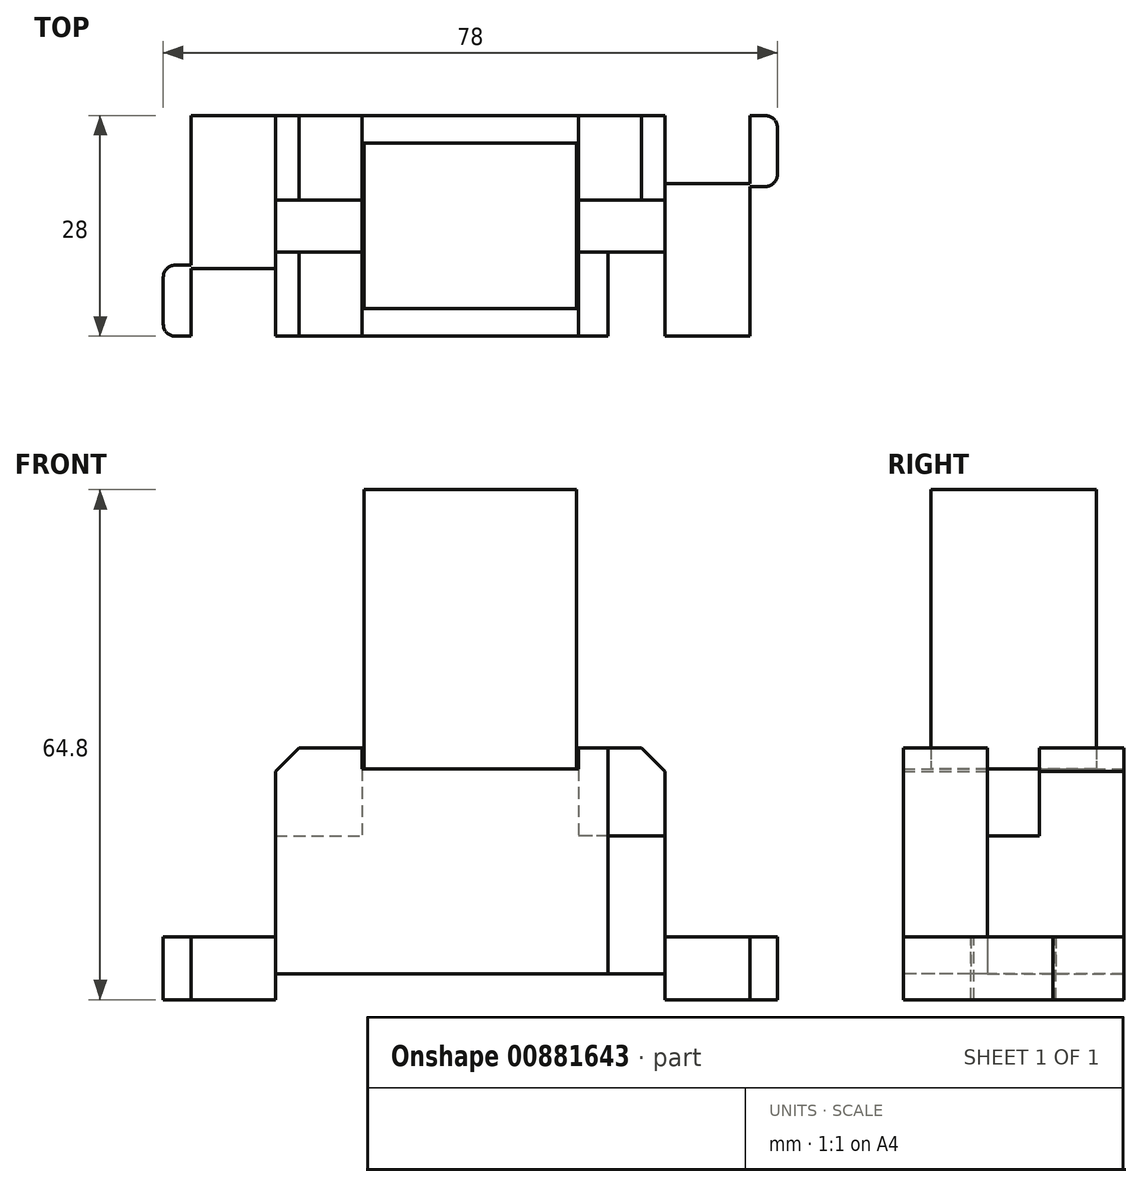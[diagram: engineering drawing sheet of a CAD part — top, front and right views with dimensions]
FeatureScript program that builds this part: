
annotation { "Feature Type Name" : "Feature", "Feature Type Description" : "" }
export const myFeature = defineFeature(function(context is Context, id is Id, definition is map)
    precondition{}
    {
        {
            var Q0;
            Q0=qCreatedBy(makeId("Top.planeOp"),FACE);
            var sketch = newSketch(context, id + "F0", { "sketchPlane" : qUnion([Q0])});
            skLineSegment(sketch, "E0.bottom", {"start": v(0, 0) * mm, "end": v(71, 0) * mm});
            skLineSegment(sketch, "E0.top", {"start": v(0, 28) * mm, "end": v(71, 28) * mm});
            skLineSegment(sketch, "E0.left", {"start": v(0, 0) * mm, "end": v(0, 28) * mm});
            skLineSegment(sketch, "E0.right", {"start": v(71, 0) * mm, "end": v(71, 28) * mm});
            skLineSegment(sketch, "E1.left", {"start": v(0, 28) * mm, "end": v(0, 19) * mm});
            skLineSegment(sketch, "E2.left", {"start": v(71, 0) * mm, "end": v(71, 9) * mm});
            skLineSegment(sketch, "E3", {"start": v(53, 28) * mm, "end": v(53, 0) * mm});
            skLineSegment(sketch, "E4", {"start": v(0, 14) * mm, "end": v(71, 14) * mm, "construction": true});
            skLineSegment(sketch, "E5", {"start": v(35.5, 28) * mm, "end": v(35.5, 0) * mm, "construction": true});
            skLineSegment(sketch, "E6.MirrorCS", {"start": v(18, 28) * mm, "end": v(18, 0) * mm});
            skLineSegment(sketch, "E7.bottom", {"start": v(71, 0) * mm, "end": v(60.25, 0) * mm});
            skLineSegment(sketch, "E7.top", {"start": v(71, 19.4) * mm, "end": v(60.25, 19.4) * mm});
            skLineSegment(sketch, "E7.left", {"start": v(71, 0) * mm, "end": v(71, 19.4) * mm});
            skLineSegment(sketch, "E7.right", {"start": v(60.25, 0) * mm, "end": v(60.25, 19.4) * mm});
            skLineSegment(sketch, "E8.bottom", {"start": v(0, 28) * mm, "end": v(10.75, 28) * mm});
            skLineSegment(sketch, "E8.top", {"start": v(0, 8.6) * mm, "end": v(10.75, 8.6) * mm});
            skLineSegment(sketch, "E8.left", {"start": v(0, 28) * mm, "end": v(0, 8.6) * mm});
            skLineSegment(sketch, "E8.right", {"start": v(10.75, 28) * mm, "end": v(10.75, 8.6) * mm});
            skLineSegment(sketch, "E9.MirrorCS", {"start": v(0, 9) * mm, "end": v(-3.5, 9) * mm});
            skLineSegment(sketch, "E10.MirrorCS", {"start": v(-3.5, 0) * mm, "end": v(-3.5, 9) * mm});
            skLineSegment(sketch, "E11.MirrorCS", {"start": v(0, 0) * mm, "end": v(-3.5, 0) * mm});
            skLineSegment(sketch, "E12.MirrorCS", {"start": v(71, 19) * mm, "end": v(74.5, 19) * mm});
            skLineSegment(sketch, "E13.MirrorCS", {"start": v(74.5, 28) * mm, "end": v(74.5, 19) * mm});
            skLineSegment(sketch, "E14.MirrorCS", {"start": v(71, 28) * mm, "end": v(74.5, 28) * mm});
            skLineSegment(sketch, "E15.bottom", {"start": v(60.25, 0) * mm, "end": v(49.25, 0) * mm});
            skLineSegment(sketch, "E15.top", {"start": v(60.25, 10.7) * mm, "end": v(49.25, 10.7) * mm});
            skLineSegment(sketch, "E15.left", {"start": v(60.25, 0) * mm, "end": v(60.25, 10.7) * mm});
            skLineSegment(sketch, "E15.right", {"start": v(49.25, 0) * mm, "end": v(49.25, 10.7) * mm});
            skLineSegment(sketch, "E16.MirrorCS", {"start": v(21.75, 0) * mm, "end": v(21.75, 10.7) * mm});
            skLineSegment(sketch, "E17.MirrorCS", {"start": v(10.75, 10.7) * mm, "end": v(21.75, 10.7) * mm});
            skLineSegment(sketch, "E18.MirrorCS", {"start": v(10.75, 17.3) * mm, "end": v(21.75, 17.3) * mm});
            skLineSegment(sketch, "E19.MirrorCS", {"start": v(21.75, 28) * mm, "end": v(21.75, 17.3) * mm});
            skLineSegment(sketch, "E20.MirrorCS", {"start": v(60.25, 17.3) * mm, "end": v(49.25, 17.3) * mm});
            skLineSegment(sketch, "E21.MirrorCS", {"start": v(49.25, 28) * mm, "end": v(49.25, 17.3) * mm});
            skLineSegment(sketch, "E22", {"start": v(10.75, 8.6) * mm, "end": v(10.75, 0) * mm});
            skLineSegment(sketch, "E23", {"start": v(60.25, 19.4) * mm, "end": v(60.25, 28) * mm});
            skLineSegment(sketch, "E24", {"start": v(49.25, 17.3) * mm, "end": v(49.25, 10.7) * mm});
            skLineSegment(sketch, "E25", {"start": v(21.75, 17.3) * mm, "end": v(21.75, 10.7) * mm});
            skLineSegment(sketch, "E26.bottom", {"start": v(22, 24.5) * mm, "end": v(49, 24.5) * mm});
            skLineSegment(sketch, "E26.top", {"start": v(22, 3.5) * mm, "end": v(49, 3.5) * mm});
            skLineSegment(sketch, "E26.left", {"start": v(22, 24.5) * mm, "end": v(22, 3.5) * mm});
            skLineSegment(sketch, "E26.right", {"start": v(49, 24.5) * mm, "end": v(49, 3.5) * mm});
            skPoint(sketch, "E26.middle", {"position": v(35.5, 14) * mm});
            skSolve(sketch);
        }
        {
            var Q0;
            {var subQ1=sQuery(id+"F0.wireOp",EDGE,"E0.left");Q0=makeQuery(id+"F0.imprint","IMPRINT",FACE,{"disambiguationData":[TD([[makeQuery(id+"F0.imprint","IMPRINT",EDGE,{"derivedFrom":subQ1}),1.0]])]});}
            var Q1;
            {var subQ0=sQuery(id+"F0.wireOp",EDGE,"E0.left");Q1=makeQuery(id+"F0.imprint","IMPRINT",FACE,{"disambiguationData":[TD([[makeQuery(id+"F0.imprint","IMPRINT",EDGE,{"derivedFrom":subQ0}),-1.0]])]});}
            var Q2;
            {var subQ3=sQuery(id+"F0.wireOp",EDGE,"E8.bottom");Q2=makeQuery(id+"F0.imprint","IMPRINT",FACE,{"disambiguationData":[TD([[makeQuery(id+"F0.imprint","IMPRINT",EDGE,{"derivedFrom":subQ3}),-1.0]])]});}
            var Q3;
            {var subQ2=sQuery(id+"F0.wireOp",EDGE,"E0.right");Q3=makeQuery(id+"F0.imprint","IMPRINT",FACE,{"disambiguationData":[TD([[makeQuery(id+"F0.imprint","IMPRINT",EDGE,{"derivedFrom":subQ2}),-1.0]])]});}
            var Q4;
            {var subQ0=sQuery(id+"F0.wireOp",EDGE,"E0.right");Q4=makeQuery(id+"F0.imprint","IMPRINT",FACE,{"disambiguationData":[TD([[makeQuery(id+"F0.imprint","IMPRINT",EDGE,{"derivedFrom":subQ0}),1.0]])]});}
            var Q5;
            {var subQ3=sQuery(id+"F0.wireOp",EDGE,"E7.bottom");Q5=makeQuery(id+"F0.imprint","IMPRINT",FACE,{"disambiguationData":[TD([[makeQuery(id+"F0.imprint","IMPRINT",EDGE,{"derivedFrom":subQ3}),-1.0]])]});}
            extrude(context, id + "F1", {"entities" : qUnion([Q0, Q1, Q2, Q3, Q4, Q5]), "oppositeDirection" : true, "depth" : 3.3 * mm, "offsetDistance" : 25 * mm});
        }
        {
            var Q0;
            {var subQ5=sQuery(id+"F0.wireOp",EDGE,"E25");Q0=makeQuery(id+"F0.imprint","IMPRINT",FACE,{"disambiguationData":[TD([[makeQuery(id+"F0.imprint","IMPRINT",EDGE,{"derivedFrom":subQ5}),-1.0]])]});}
            var Q1;
            {var subQ3=sQuery(id+"F0.wireOp",EDGE,"E8.bottom");Q1=makeQuery(id+"F0.imprint","IMPRINT",FACE,{"disambiguationData":[TD([[makeQuery(id+"F0.imprint","IMPRINT",EDGE,{"derivedFrom":subQ3}),-1.0]])]});}
            var Q2;
            {var subQ0=sQuery(id+"F0.wireOp",EDGE,"E0.right");Q2=makeQuery(id+"F0.imprint","IMPRINT",FACE,{"disambiguationData":[TD([[makeQuery(id+"F0.imprint","IMPRINT",EDGE,{"derivedFrom":subQ0}),1.0]])]});}
            var Q3;
            {var subQ2=sQuery(id+"F0.wireOp",EDGE,"E0.right");Q3=makeQuery(id+"F0.imprint","IMPRINT",FACE,{"disambiguationData":[TD([[makeQuery(id+"F0.imprint","IMPRINT",EDGE,{"derivedFrom":subQ2}),-1.0]])]});}
            var Q4;
            {var subQ5=sQuery(id+"F0.wireOp",EDGE,"E15.right");Q4=makeQuery(id+"F0.imprint","IMPRINT",FACE,{"disambiguationData":[TD([[makeQuery(id+"F0.imprint","IMPRINT",EDGE,{"derivedFrom":subQ5}),-1.0]])]});}
            var Q5;
            {var subQ0=sQuery(id+"F0.wireOp",EDGE,"E18.MirrorCS");var subQ1=sQuery(id+"F0.wireOp",EDGE,"E6.MirrorCS");var subQ2=makeQuery(id+"F0.imprint","INTERSECT",VERTEX,{"derivedFrom":[subQ1,subQ0]});Q5=makeQuery(id+"F0.imprint","IMPRINT",FACE,{"disambiguationData":[TD([[makeQuery(id+"F0.imprint","IMPRINT",EDGE,{"disambiguationData":[TD([[subQ2,-1.0]])],"derivedFrom":subQ1}),-1.0]])]});}
            var Q6;
            {var subQ3=sQuery(id+"F0.wireOp",EDGE,"E16.MirrorCS");Q6=makeQuery(id+"F0.imprint","IMPRINT",FACE,{"disambiguationData":[TD([[makeQuery(id+"F0.imprint","IMPRINT",EDGE,{"derivedFrom":subQ3}),1.0]])]});}
            var Q7;
            {var subQ1=sQuery(id+"F0.wireOp",EDGE,"E0.left");Q7=makeQuery(id+"F0.imprint","IMPRINT",FACE,{"disambiguationData":[TD([[makeQuery(id+"F0.imprint","IMPRINT",EDGE,{"derivedFrom":subQ1}),1.0]])]});}
            var Q8;
            {var subQ0=sQuery(id+"F0.wireOp",EDGE,"E20.MirrorCS");var subQ1=sQuery(id+"F0.wireOp",EDGE,"E3");var subQ2=makeQuery(id+"F0.imprint","INTERSECT",VERTEX,{"derivedFrom":[subQ1,subQ0]});Q8=makeQuery(id+"F0.imprint","IMPRINT",FACE,{"disambiguationData":[TD([[makeQuery(id+"F0.imprint","IMPRINT",EDGE,{"disambiguationData":[TD([[subQ2,-1.0]])],"derivedFrom":subQ1}),1.0]])]});}
            var Q9;
            {var subQ3=sQuery(id+"F0.wireOp",EDGE,"E21.MirrorCS");Q9=makeQuery(id+"F0.imprint","IMPRINT",FACE,{"disambiguationData":[TD([[makeQuery(id+"F0.imprint","IMPRINT",EDGE,{"derivedFrom":subQ3}),1.0]])]});}
            var Q10;
            {var subQ5=sQuery(id+"F0.wireOp",EDGE,"E15.left");Q10=makeQuery(id+"F0.imprint","IMPRINT",FACE,{"disambiguationData":[TD([[makeQuery(id+"F0.imprint","IMPRINT",EDGE,{"derivedFrom":subQ5}),1.0]])]});}
            var Q11;
            {var subQ3=sQuery(id+"F0.wireOp",EDGE,"E19.MirrorCS");Q11=makeQuery(id+"F0.imprint","IMPRINT",FACE,{"disambiguationData":[TD([[makeQuery(id+"F0.imprint","IMPRINT",EDGE,{"derivedFrom":subQ3}),-1.0]])]});}
            var Q12;
            {var subQ3=sQuery(id+"F0.wireOp",EDGE,"E7.bottom");Q12=makeQuery(id+"F0.imprint","IMPRINT",FACE,{"disambiguationData":[TD([[makeQuery(id+"F0.imprint","IMPRINT",EDGE,{"derivedFrom":subQ3}),-1.0]])]});}
            var Q13;
            Q13=makeQuery(id+"F0.imprint","IMPRINT",FACE,{"disambiguationData":[TD([[makeQuery(id+"F0.imprint","IMPRINT",EDGE,{"derivedFrom":sQuery(id+"F0.wireOp",EDGE,"E26.bottom")}),-1.0]])]});
            var Q14;
            {var subQ0=sQuery(id+"F0.wireOp",EDGE,"E0.left");Q14=makeQuery(id+"F0.imprint","IMPRINT",FACE,{"disambiguationData":[TD([[makeQuery(id+"F0.imprint","IMPRINT",EDGE,{"derivedFrom":subQ0}),-1.0]])]});}
            var Q15;
            {var subQ2=sQuery(id+"F0.wireOp",EDGE,"E15.right");Q15=makeQuery(id+"F0.imprint","IMPRINT",FACE,{"disambiguationData":[TD([[makeQuery(id+"F0.imprint","IMPRINT",EDGE,{"derivedFrom":subQ2}),1.0]])]});}
            var Q16;
            {var subQ7=sQuery(id+"F0.wireOp",EDGE,"E23");Q16=makeQuery(id+"F0.imprint","IMPRINT",FACE,{"disambiguationData":[TD([[makeQuery(id+"F0.imprint","IMPRINT",EDGE,{"derivedFrom":subQ7}),1.0]])]});}
            var Q17;
            {var subQ5=sQuery(id+"F0.wireOp",EDGE,"E22");Q17=makeQuery(id+"F0.imprint","IMPRINT",FACE,{"disambiguationData":[TD([[makeQuery(id+"F0.imprint","IMPRINT",EDGE,{"derivedFrom":subQ5}),1.0]])]});}
            var Q18;
            {var subQ5=sQuery(id+"F0.wireOp",EDGE,"E24");Q18=makeQuery(id+"F0.imprint","IMPRINT",FACE,{"disambiguationData":[TD([[makeQuery(id+"F0.imprint","IMPRINT",EDGE,{"derivedFrom":subQ5}),1.0]])]});}
            var Q19;
            {var subQ1=sQuery(id+"F0.wireOp",EDGE,"E0.top");var subQ3=sQuery(id+"F0.wireOp",EDGE,"E6.MirrorCS");var subQ4=makeQuery(id+"F0.imprint","INTERSECT",VERTEX,{"derivedFrom":[subQ1,subQ3]});Q19=makeQuery(id+"F0.imprint","IMPRINT",FACE,{"disambiguationData":[TD([[makeQuery(id+"F0.imprint","IMPRINT",EDGE,{"disambiguationData":[TD([[subQ4,-1.0]])],"derivedFrom":subQ3}),-1.0]])]});}
            extrude(context, id + "F2", {"entities" : qUnion([Q0, Q1, Q2, Q3, Q4, Q5, Q6, Q7, Q8, Q9, Q10, Q11, Q12, Q13, Q14, Q15, Q16, Q17, Q18, Q19]), "operationType" : NewBodyOperationType.ADD, "depth" : (8 - 3.3) * mm, "offsetDistance" : 25 * mm});
        }
        {
            var Q0;
            {var subQ3=sQuery(id+"F0.wireOp",EDGE,"E8.bottom");Q0=makeQuery(id+"F0.imprint","IMPRINT",FACE,{"disambiguationData":[TD([[makeQuery(id+"F0.imprint","IMPRINT",EDGE,{"derivedFrom":subQ3}),-1.0]])]});}
            var Q1;
            {var subQ3=sQuery(id+"F0.wireOp",EDGE,"E7.bottom");Q1=makeQuery(id+"F0.imprint","IMPRINT",FACE,{"disambiguationData":[TD([[makeQuery(id+"F0.imprint","IMPRINT",EDGE,{"derivedFrom":subQ3}),-1.0]])]});}
            var Q2;
            {var subQ0=sQuery(id+"F0.wireOp",EDGE,"E18.MirrorCS");var subQ1=sQuery(id+"F0.wireOp",EDGE,"E6.MirrorCS");var subQ2=makeQuery(id+"F0.imprint","INTERSECT",VERTEX,{"derivedFrom":[subQ1,subQ0]});Q2=makeQuery(id+"F0.imprint","IMPRINT",FACE,{"disambiguationData":[TD([[makeQuery(id+"F0.imprint","IMPRINT",EDGE,{"disambiguationData":[TD([[subQ2,-1.0]])],"derivedFrom":subQ1}),-1.0]])]});}
            var Q3;
            {var subQ5=sQuery(id+"F0.wireOp",EDGE,"E25");Q3=makeQuery(id+"F0.imprint","IMPRINT",FACE,{"disambiguationData":[TD([[makeQuery(id+"F0.imprint","IMPRINT",EDGE,{"derivedFrom":subQ5}),-1.0]])]});}
            var Q4;
            {var subQ5=sQuery(id+"F0.wireOp",EDGE,"E24");Q4=makeQuery(id+"F0.imprint","IMPRINT",FACE,{"disambiguationData":[TD([[makeQuery(id+"F0.imprint","IMPRINT",EDGE,{"derivedFrom":subQ5}),1.0]])]});}
            var Q5;
            {var subQ0=sQuery(id+"F0.wireOp",EDGE,"E20.MirrorCS");var subQ1=sQuery(id+"F0.wireOp",EDGE,"E3");var subQ2=makeQuery(id+"F0.imprint","INTERSECT",VERTEX,{"derivedFrom":[subQ1,subQ0]});Q5=makeQuery(id+"F0.imprint","IMPRINT",FACE,{"disambiguationData":[TD([[makeQuery(id+"F0.imprint","IMPRINT",EDGE,{"disambiguationData":[TD([[subQ2,-1.0]])],"derivedFrom":subQ1}),1.0]])]});}
            extrude(context, id + "F3", {"entities" : qUnion([Q0, Q1, Q2, Q3, Q4, Q5]), "operationType" : NewBodyOperationType.ADD, "depth" : (20.8 - 3.3) * mm, "offsetDistance" : 25 * mm});
        }
        {
            var Q0;
            {var subQ1=sQuery(id+"F0.wireOp",EDGE,"E0.top");var subQ3=sQuery(id+"F0.wireOp",EDGE,"E6.MirrorCS");var subQ4=makeQuery(id+"F0.imprint","INTERSECT",VERTEX,{"derivedFrom":[subQ1,subQ3]});Q0=makeQuery(id+"F0.imprint","IMPRINT",FACE,{"disambiguationData":[TD([[makeQuery(id+"F0.imprint","IMPRINT",EDGE,{"disambiguationData":[TD([[subQ4,-1.0]])],"derivedFrom":subQ3}),-1.0]])]});}
            var Q1;
            {var subQ5=sQuery(id+"F0.wireOp",EDGE,"E22");Q1=makeQuery(id+"F0.imprint","IMPRINT",FACE,{"disambiguationData":[TD([[makeQuery(id+"F0.imprint","IMPRINT",EDGE,{"derivedFrom":subQ5}),1.0]])]});}
            var Q2;
            {var subQ3=sQuery(id+"F0.wireOp",EDGE,"E16.MirrorCS");Q2=makeQuery(id+"F0.imprint","IMPRINT",FACE,{"disambiguationData":[TD([[makeQuery(id+"F0.imprint","IMPRINT",EDGE,{"derivedFrom":subQ3}),1.0]])]});}
            var Q3;
            {var subQ3=sQuery(id+"F0.wireOp",EDGE,"E19.MirrorCS");Q3=makeQuery(id+"F0.imprint","IMPRINT",FACE,{"disambiguationData":[TD([[makeQuery(id+"F0.imprint","IMPRINT",EDGE,{"derivedFrom":subQ3}),-1.0]])]});}
            var Q4;
            {var subQ3=sQuery(id+"F0.wireOp",EDGE,"E21.MirrorCS");Q4=makeQuery(id+"F0.imprint","IMPRINT",FACE,{"disambiguationData":[TD([[makeQuery(id+"F0.imprint","IMPRINT",EDGE,{"derivedFrom":subQ3}),1.0]])]});}
            var Q5;
            {var subQ7=sQuery(id+"F0.wireOp",EDGE,"E23");Q5=makeQuery(id+"F0.imprint","IMPRINT",FACE,{"disambiguationData":[TD([[makeQuery(id+"F0.imprint","IMPRINT",EDGE,{"derivedFrom":subQ7}),1.0]])]});}
            var Q6;
            {var subQ5=sQuery(id+"F0.wireOp",EDGE,"E15.left");Q6=makeQuery(id+"F0.imprint","IMPRINT",FACE,{"disambiguationData":[TD([[makeQuery(id+"F0.imprint","IMPRINT",EDGE,{"derivedFrom":subQ5}),1.0]])]});}
            var Q7;
            {var subQ5=sQuery(id+"F0.wireOp",EDGE,"E15.right");Q7=makeQuery(id+"F0.imprint","IMPRINT",FACE,{"disambiguationData":[TD([[makeQuery(id+"F0.imprint","IMPRINT",EDGE,{"derivedFrom":subQ5}),-1.0]])]});}
            extrude(context, id + "F4", {"entities" : qUnion([Q0, Q1, Q2, Q3, Q4, Q5, Q6, Q7]), "operationType" : NewBodyOperationType.ADD, "depth" : (32 - 3.3) * mm, "offsetDistance" : 25 * mm});
        }
        {
            var Q0;
            {var subQ2=sQuery(id+"F0.wireOp",EDGE,"E15.right");Q0=makeQuery(id+"F0.imprint","IMPRINT",FACE,{"disambiguationData":[TD([[makeQuery(id+"F0.imprint","IMPRINT",EDGE,{"derivedFrom":subQ2}),1.0]])]});}
            extrude(context, id + "F5", {"entities" : qUnion([Q0]), "operationType" : NewBodyOperationType.ADD, "depth" : 26 * mm, "offsetDistance" : 25 * mm});
        }
        {
            var Q0;
            Q0=makeQuery(id+"F0.imprint","IMPRINT",FACE,{"disambiguationData":[TD([[makeQuery(id+"F0.imprint","IMPRINT",EDGE,{"derivedFrom":sQuery(id+"F0.wireOp",EDGE,"E26.bottom")}),-1.0]])]});
            extrude(context, id + "F6", {"entities" : qUnion([Q0]), "operationType" : NewBodyOperationType.ADD, "depth" : 61.5 * mm, "offsetDistance" : 25 * mm});
        }
        {
            var Q0;
            Q0=makeQuery(id+"F4.opExtrude","CAP_EDGE",EDGE,{"disambiguationData":[OSD([sQuery(id+"F0.wireOp",EDGE,"E8.right")])],"isStart":false});
            var Q1;
            Q1=makeQuery(id+"F4.opExtrude","CAP_EDGE",EDGE,{"disambiguationData":[OSD([sQuery(id+"F0.wireOp",EDGE,"E8.right"),sQuery(id+"F0.wireOp",EDGE,"E22")])],"isStart":false});
            var Q2;
            Q2=makeQuery(id+"F4.opExtrude","CAP_EDGE",EDGE,{"disambiguationData":[OSD([sQuery(id+"F0.wireOp",EDGE,"E7.right"),sQuery(id+"F0.wireOp",EDGE,"E23")])],"isStart":false});
            var Q3;
            Q3=makeQuery(id+"F4.opExtrude","CAP_EDGE",EDGE,{"disambiguationData":[OSD([sQuery(id+"F0.wireOp",EDGE,"E15.left")])],"isStart":false});
            var Q4;
            Q4=makeQuery(id+"F3.opExtrude","CAP_EDGE",EDGE,{"disambiguationData":[OSD([sQuery(id+"F0.wireOp",EDGE,"E8.left")])],"isStart":false});
            var Q5;
            Q5=makeQuery(id+"F3.opExtrude","CAP_EDGE",EDGE,{"disambiguationData":[OSD([sQuery(id+"F0.wireOp",EDGE,"E7.left")])],"isStart":false});
            chamfer(context, id + "F7", {"entities" : qUnion([Q0, Q1, Q2, Q3, Q4, Q5]), "width" : 3 * mm, "tangentPropagation" : true});
        }
        {
            var Q0;
            {var subQ0=sQuery(id+"F0.wireOp",EDGE,"E11.MirrorCS");var subQ1=sQuery(id+"F0.wireOp",EDGE,"E10.MirrorCS");Q0=makeQuery(id+"F2.boolean.opBoolean","MERGE",EDGE,{"derivedFrom":[makeQuery(id+"F1.opExtrude","SWEPT_EDGE",EDGE,{"disambiguationData":[OSD([subQ1,subQ0])]}),makeQuery(id+"F2.opExtrude","SWEPT_EDGE",EDGE,{"disambiguationData":[OSD([subQ1,subQ0])]})]});}
            var Q1;
            {var subQ0=sQuery(id+"F0.wireOp",EDGE,"E14.MirrorCS");var subQ1=sQuery(id+"F0.wireOp",EDGE,"E13.MirrorCS");Q1=makeQuery(id+"F2.boolean.opBoolean","MERGE",EDGE,{"derivedFrom":[makeQuery(id+"F1.opExtrude","SWEPT_EDGE",EDGE,{"disambiguationData":[OSD([subQ1,subQ0])]}),makeQuery(id+"F2.opExtrude","SWEPT_EDGE",EDGE,{"disambiguationData":[OSD([subQ1,subQ0])]})]});}
            var Q2;
            {var subQ0=sQuery(id+"F0.wireOp",EDGE,"E13.MirrorCS");var subQ1=sQuery(id+"F0.wireOp",EDGE,"E12.MirrorCS");Q2=makeQuery(id+"F2.boolean.opBoolean","MERGE",EDGE,{"derivedFrom":[makeQuery(id+"F1.opExtrude","SWEPT_EDGE",EDGE,{"disambiguationData":[OSD([subQ1,subQ0])]}),makeQuery(id+"F2.opExtrude","SWEPT_EDGE",EDGE,{"disambiguationData":[OSD([subQ1,subQ0])]})]});}
            var Q3;
            {var subQ0=sQuery(id+"F0.wireOp",EDGE,"E10.MirrorCS");var subQ1=sQuery(id+"F0.wireOp",EDGE,"E9.MirrorCS");Q3=makeQuery(id+"F2.boolean.opBoolean","MERGE",EDGE,{"derivedFrom":[makeQuery(id+"F1.opExtrude","SWEPT_EDGE",EDGE,{"disambiguationData":[OSD([subQ1,subQ0])]}),makeQuery(id+"F2.opExtrude","SWEPT_EDGE",EDGE,{"disambiguationData":[OSD([subQ1,subQ0])]})]});}
            fillet(context, id + "F8", {"entities" : qUnion([Q0, Q1, Q2, Q3]), "radius" : 1.5 * mm, "tangentPropagation" : true, "allowEdgeOverflow" : false});
        }
    });
